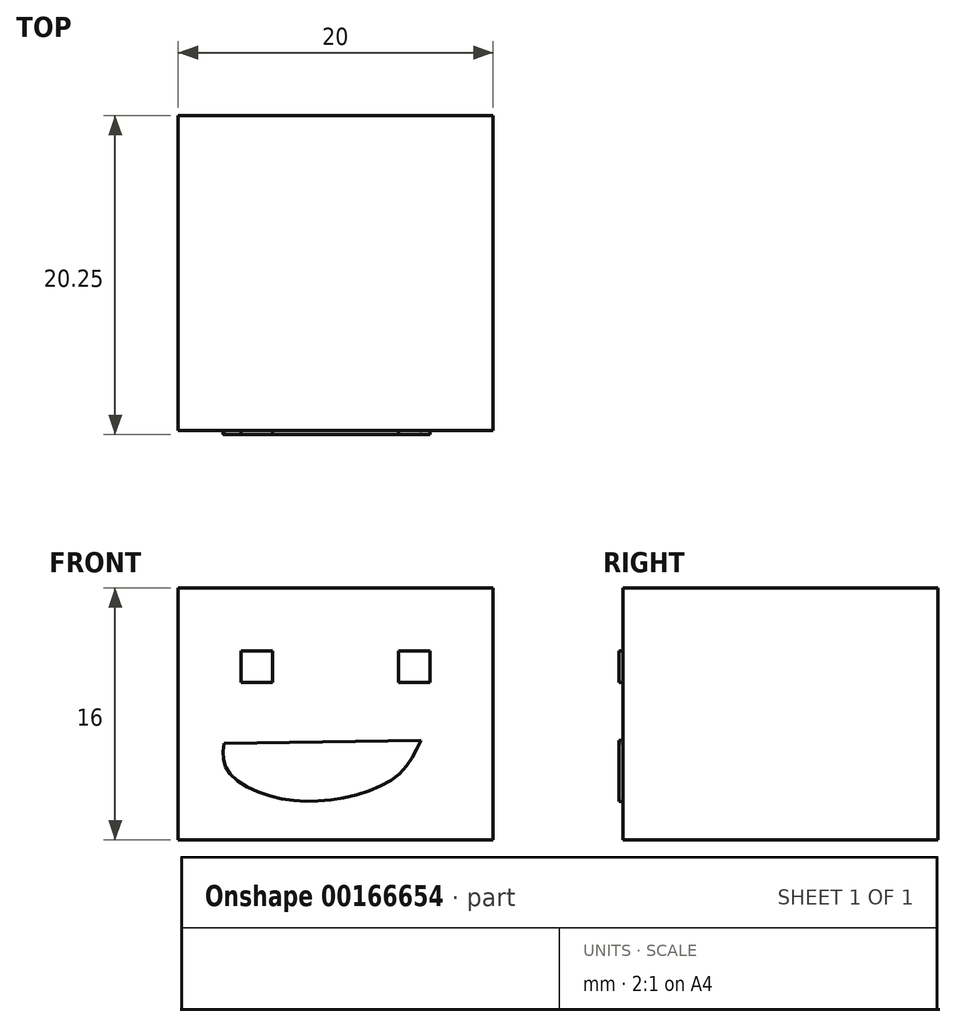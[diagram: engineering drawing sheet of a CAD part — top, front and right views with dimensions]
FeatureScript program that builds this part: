
annotation { "Feature Type Name" : "Feature", "Feature Type Description" : "" }
export const myFeature = defineFeature(function(context is Context, id is Id, definition is map)
    precondition{}
    {
        {
            var Q0;
            Q0=qCreatedBy(makeId("Front.planeOp"),FACE);
            var sketch = newSketch(context, id + "F0", { "sketchPlane" : qUnion([Q0])});
            skLineSegment(sketch, "E0.bottom", {"start": v(-10, 8) * mm, "end": v(10, 8) * mm});
            skLineSegment(sketch, "E0.top", {"start": v(-10, -8) * mm, "end": v(10, -8) * mm});
            skLineSegment(sketch, "E0.left", {"start": v(-10, 8) * mm, "end": v(-10, -8) * mm});
            skLineSegment(sketch, "E0.right", {"start": v(10, 8) * mm, "end": v(10, -8) * mm});
            skPoint(sketch, "E0.middle", {"position": v(0, 0) * mm});
            skSolve(sketch);
        }
        {
            var Q0;
            Q0 = qSketchRegion(id + "F0", true);
            extrude(context, id + "F1", {"entities" : qUnion([Q0]), "depth" : 20 * mm});
        }
        {
            var Q0;
            Q0=makeQuery(id+"F1.opExtrude","CAP_FACE",FACE,{"disambiguationData":[OSD([sQuery(id+"F0.wireOp",EDGE,"E0.bottom"),sQuery(id+"F0.wireOp",EDGE,"E0.top"),sQuery(id+"F0.wireOp",EDGE,"E0.left"),sQuery(id+"F0.wireOp",EDGE,"E0.right")])],"isStart":false});
            var sketch = newSketch(context, id + "F2", { "sketchPlane" : qUnion([Q0])});
            skLineSegment(sketch, "E1", {"start": v(6, 4) * mm, "end": v(6, 2) * mm});
            skLineSegment(sketch, "E2", {"start": v(6, 4) * mm, "end": v(4, 4) * mm});
            skLineSegment(sketch, "E3", {"start": v(4, 4) * mm, "end": v(4, 2) * mm});
            skLineSegment(sketch, "E4", {"start": v(4, 2) * mm, "end": v(6, 2) * mm});
            skLineSegment(sketch, "E5", {"start": v(-6, 4) * mm, "end": v(-6, 2) * mm});
            skLineSegment(sketch, "E6", {"start": v(-6, 2) * mm, "end": v(-4, 2) * mm});
            skLineSegment(sketch, "E7", {"start": v(-4, 2) * mm, "end": v(-4, 4) * mm});
            skLineSegment(sketch, "E8", {"start": v(-4, 4) * mm, "end": v(-6, 4) * mm});
            skSolve(sketch);
        }
        {
            var Q0;
            Q0 = qSketchRegion(id + "F2", true);
            extrude(context, id + "F3", {"entities" : qUnion([Q0]), "depth" : 0.25 * mm});
        }
        {
            var Q0;
            Q0=makeQuery(id+"F1.opExtrude","CAP_FACE",FACE,{"disambiguationData":[OSD([sQuery(id+"F0.wireOp",EDGE,"E0.bottom"),sQuery(id+"F0.wireOp",EDGE,"E0.top"),sQuery(id+"F0.wireOp",EDGE,"E0.left"),sQuery(id+"F0.wireOp",EDGE,"E0.right")])],"isStart":false});
            var sketch = newSketch(context, id + "F4", { "sketchPlane" : qUnion([Q0])});
            skPoint(sketch, "E9.3.internal.snap0", {"position": v(0, -8) * mm});
            skFitSpline(sketch, "E9", {"points": [v(-7.1, -1.87) * mm, v(-6.9, -3.55) * mm, v(-4.1, -5.23) * mm, v(0, -5.41) * mm, v(3.92, -3.92) * mm, v(5.41, -1.68) * mm], "startDerivative": vector(-1.32, -11.78) * mm, "endDerivative": vector(5.97, 13.04) * mm});
            skLineSegment(sketch, "E10", {"start": v(5.41, -1.68) * mm, "end": v(-7.1, -1.87) * mm});
            skSolve(sketch);
        }
        {
            var Q0;
            Q0 = qSketchRegion(id + "F4", true);
            extrude(context, id + "F5", {"entities" : qUnion([Q0]), "depth" : 0.25 * mm});
        }
    });
